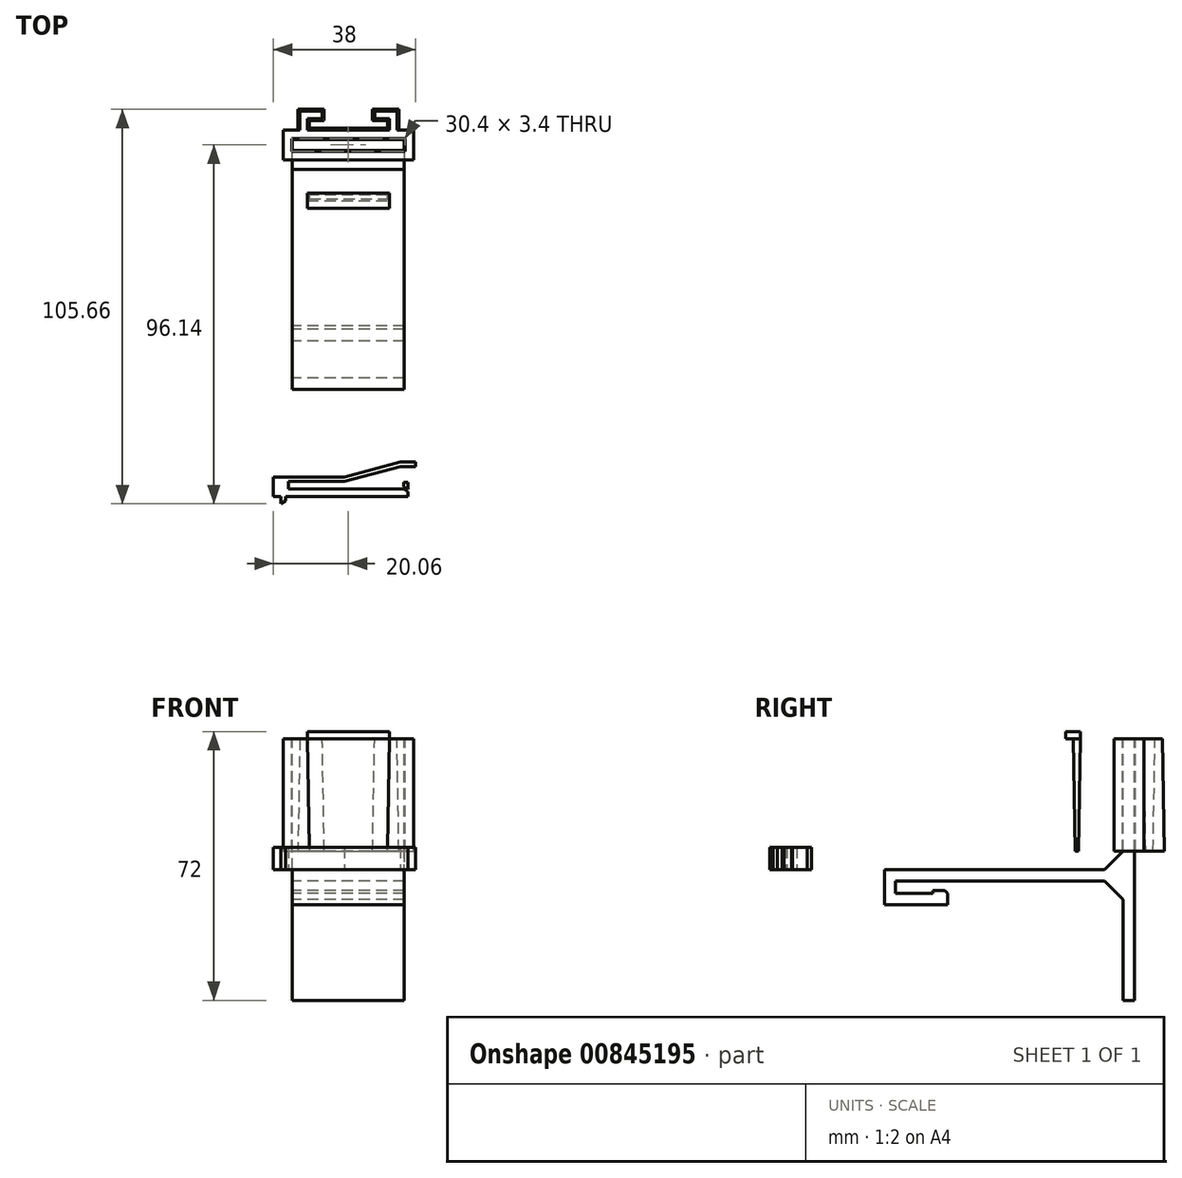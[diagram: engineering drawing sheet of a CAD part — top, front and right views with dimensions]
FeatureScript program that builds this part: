
annotation { "Feature Type Name" : "Feature", "Feature Type Description" : "" }
export const myFeature = defineFeature(function(context is Context, id is Id, definition is map)
    precondition{}
    {
        {
            var Q0;
            Q0=qCreatedBy(makeId("Right.planeOp"),FACE);
            var sketch = newSketch(context, id + "F0", { "sketchPlane" : qUnion([Q0])});
            skLineSegment(sketch, "E0.bottom", {"start": v(0, 0) * mm, "end": v(64, 0) * mm});
            skLineSegment(sketch, "E0.top", {"start": v(0, -3) * mm, "end": v(64, -3) * mm});
            skLineSegment(sketch, "E0.left", {"start": v(0, 0) * mm, "end": v(0, -3) * mm});
            skLineSegment(sketch, "E0.right", {"start": v(64, 0) * mm, "end": v(64, -3) * mm});
            skLineSegment(sketch, "E1.bottom", {"start": v(64, 0) * mm, "end": v(67, 0) * mm});
            skLineSegment(sketch, "E1.top", {"start": v(64, -35) * mm, "end": v(67, -35) * mm});
            skLineSegment(sketch, "E1.left", {"start": v(64, 0) * mm, "end": v(64, -35) * mm});
            skLineSegment(sketch, "E1.right", {"start": v(67, 0) * mm, "end": v(67, -35) * mm});
            skLineSegment(sketch, "E2.bottom", {"start": v(0, -3) * mm, "end": v(3, -3) * mm});
            skLineSegment(sketch, "E2.top", {"start": v(0, -9.4) * mm, "end": v(3, -9.4) * mm});
            skLineSegment(sketch, "E2.left", {"start": v(0, -3) * mm, "end": v(0, -9.4) * mm});
            skLineSegment(sketch, "E2.right", {"start": v(3, -3) * mm, "end": v(3, -9.4) * mm});
            skLineSegment(sketch, "E3.bottom", {"start": v(3, -9.4) * mm, "end": v(17, -9.4) * mm});
            skLineSegment(sketch, "E3.top", {"start": v(3, -6.4) * mm, "end": v(17, -6.4) * mm});
            skLineSegment(sketch, "E3.left", {"start": v(3, -9.4) * mm, "end": v(3, -6.4) * mm});
            skLineSegment(sketch, "E3.right", {"start": v(17, -9.4) * mm, "end": v(17, -6.4) * mm});
            skLineSegment(sketch, "E4.top", {"start": v(64, 35) * mm, "end": v(67, 35) * mm});
            skLineSegment(sketch, "E4.left", {"start": v(64, 0) * mm, "end": v(64, 35) * mm});
            skLineSegment(sketch, "E4.right", {"start": v(67, 0) * mm, "end": v(67, 35) * mm});
            skLineSegment(sketch, "E5.bottom", {"start": v(64, 0) * mm, "end": v(59, 0) * mm});
            skLineSegment(sketch, "E5.top", {"start": v(64, 5) * mm, "end": v(59, 5) * mm});
            skLineSegment(sketch, "E5.left", {"start": v(64, 0) * mm, "end": v(64, 5) * mm});
            skLineSegment(sketch, "E5.right", {"start": v(59, 0) * mm, "end": v(59, 5) * mm});
            skLineSegment(sketch, "E6.bottom", {"start": v(17, -6.4) * mm, "end": v(13, -6.4) * mm});
            skLineSegment(sketch, "E6.top", {"start": v(17, -5.6) * mm, "end": v(13, -5.6) * mm});
            skLineSegment(sketch, "E6.left", {"start": v(17, -6.4) * mm, "end": v(17, -5.6) * mm});
            skLineSegment(sketch, "E6.right", {"start": v(13, -6.4) * mm, "end": v(13, -5.6) * mm});
            skLineSegment(sketch, "E7.bottom", {"start": v(64, -3) * mm, "end": v(59, -3) * mm});
            skLineSegment(sketch, "E7.top", {"start": v(64, -8) * mm, "end": v(59, -8) * mm});
            skLineSegment(sketch, "E7.left", {"start": v(64, -3) * mm, "end": v(64, -8) * mm});
            skLineSegment(sketch, "E7.right", {"start": v(59, -3) * mm, "end": v(59, -8) * mm});
            skSolve(sketch);
        }
        {
            var Q0;
            Q0 = qSketchRegion(id + "F0", true);
            extrude(context, id + "F1", {"entities" : qUnion([Q0]), "depth" : 30 * mm, "offsetDistance" : 25 * mm});
        }
        {
            var Q0;
            Q0=qCreatedBy(makeId("Top.planeOp"),FACE);
            cPlane(context, id + "F2", {"entities" : qUnion([Q0]), "cplaneType" : CPlaneType.OFFSET, "offset" : 35 * mm, "width" : 150 * mm, "height" : 150 * mm});
        }
        {
            var Q0;
            Q0=qCreatedBy(id+"F2.planeOp",FACE);
            var sketch = newSketch(context, id + "F3", { "sketchPlane" : qUnion([Q0])});
            skLineSegment(sketch, "E8.0.0", {"start": v(0, 67) * mm, "end": v(0, 64) * mm, "construction": true});
            skLineSegment(sketch, "E8.0.1", {"start": v(0, 64) * mm, "end": v(30, 64) * mm, "construction": true});
            skLineSegment(sketch, "E8.0.2", {"start": v(30, 64) * mm, "end": v(30, 67) * mm, "construction": true});
            skLineSegment(sketch, "E8.0.3", {"start": v(30, 67) * mm, "end": v(0, 67) * mm, "construction": true});
            skLineSegment(sketch, "E9", {"start": v(15, 67) * mm, "end": v(15, 64) * mm, "construction": true});
            skLineSegment(sketch, "E10", {"start": v(0, 65.5) * mm, "end": v(30, 65.5) * mm, "construction": true});
            skLineSegment(sketch, "E11.bottom", {"start": v(-0.2, 67.2) * mm, "end": v(30.2, 67.2) * mm});
            skLineSegment(sketch, "E11.top", {"start": v(-0.2, 63.8) * mm, "end": v(30.2, 63.8) * mm});
            skLineSegment(sketch, "E11.left", {"start": v(-0.2, 67.2) * mm, "end": v(-0.2, 63.8) * mm});
            skLineSegment(sketch, "E11.right", {"start": v(30.2, 67.2) * mm, "end": v(30.2, 63.8) * mm});
            skPoint(sketch, "E11.middle", {"position": v(15, 65.5) * mm});
            skLineSegment(sketch, "E12.bottom", {"start": v(-2.5, 69.5) * mm, "end": v(32.5, 69.5) * mm});
            skLineSegment(sketch, "E12.top", {"start": v(-2.5, 61.5) * mm, "end": v(32.5, 61.5) * mm});
            skLineSegment(sketch, "E12.left", {"start": v(-2.5, 69.5) * mm, "end": v(-2.5, 61.5) * mm});
            skLineSegment(sketch, "E12.right", {"start": v(32.5, 69.5) * mm, "end": v(32.5, 61.5) * mm});
            skLineSegment(sketch, "E13.bottom", {"start": v(4, 50.55) * mm, "end": v(26, 50.55) * mm});
            skLineSegment(sketch, "E13.top", {"start": v(4, 52.55) * mm, "end": v(26, 52.55) * mm});
            skLineSegment(sketch, "E13.left", {"start": v(4, 50.55) * mm, "end": v(4, 52.55) * mm});
            skLineSegment(sketch, "E13.right", {"start": v(26, 50.55) * mm, "end": v(26, 52.55) * mm});
            skPoint(sketch, "E13.middle", {"position": v(15, 51.55) * mm});
            skPoint(sketch, "E13.middle.positionSnap0", {"position": v(15, 61.5) * mm});
            skPoint(sketch, "E13.centerSnap0", {"position": v(15, 61.5) * mm});
            skLineSegment(sketch, "E14.top", {"start": v(4, 48.55) * mm, "end": v(26, 48.55) * mm});
            skLineSegment(sketch, "E14.left", {"start": v(4, 50.55) * mm, "end": v(4, 48.55) * mm});
            skLineSegment(sketch, "E14.right", {"start": v(26, 50.55) * mm, "end": v(26, 48.55) * mm});
            skLineSegment(sketch, "E15.bottom", {"start": v(2, 69.5) * mm, "end": v(4, 69.5) * mm});
            skLineSegment(sketch, "E15.top", {"start": v(2, 72.5) * mm, "end": v(4, 72.5) * mm});
            skLineSegment(sketch, "E15.left", {"start": v(2, 69.5) * mm, "end": v(2, 72.5) * mm});
            skLineSegment(sketch, "E15.right", {"start": v(4, 69.5) * mm, "end": v(4, 72.5) * mm});
            skLineSegment(sketch, "E16.bottom", {"start": v(26, 69.5) * mm, "end": v(28, 69.5) * mm});
            skLineSegment(sketch, "E16.top", {"start": v(26, 72.5) * mm, "end": v(28, 72.5) * mm});
            skLineSegment(sketch, "E16.left", {"start": v(26, 69.5) * mm, "end": v(26, 72.5) * mm});
            skLineSegment(sketch, "E16.right", {"start": v(28, 69.5) * mm, "end": v(28, 72.5) * mm});
            skLineSegment(sketch, "E17.bottom", {"start": v(2, 72.5) * mm, "end": v(8, 72.5) * mm});
            skLineSegment(sketch, "E17.top", {"start": v(2, 74.5) * mm, "end": v(8, 74.5) * mm});
            skLineSegment(sketch, "E17.left", {"start": v(2, 72.5) * mm, "end": v(2, 74.5) * mm});
            skLineSegment(sketch, "E17.right", {"start": v(8, 72.5) * mm, "end": v(8, 74.5) * mm});
            skLineSegment(sketch, "E18.bottom", {"start": v(28, 72.5) * mm, "end": v(22, 72.5) * mm});
            skLineSegment(sketch, "E18.top", {"start": v(28, 74.5) * mm, "end": v(22, 74.5) * mm});
            skLineSegment(sketch, "E18.left", {"start": v(28, 72.5) * mm, "end": v(28, 74.5) * mm});
            skLineSegment(sketch, "E18.right", {"start": v(22, 72.5) * mm, "end": v(22, 74.5) * mm});
            skLineSegment(sketch, "E19.bottom", {"start": v(2, 69.5) * mm, "end": v(28, 69.5) * mm});
            skLineSegment(sketch, "E19.top", {"start": v(2, 68.5) * mm, "end": v(28, 68.5) * mm});
            skLineSegment(sketch, "E19.left", {"start": v(2, 69.5) * mm, "end": v(2, 68.5) * mm});
            skLineSegment(sketch, "E19.right", {"start": v(28, 69.5) * mm, "end": v(28, 68.5) * mm});
            skSolve(sketch);
        }
        {
            var Q0;
            Q0=makeQuery(id+"F3.imprint","IMPRINT",FACE,{"disambiguationData":[TD([[makeQuery(id+"F3.imprint","IMPRINT",EDGE,{"derivedFrom":sQuery(id+"F3.wireOp",EDGE,"E11.bottom")}),1.0]])]});
            var Q1;
            Q1=makeQuery(id+"F3.imprint","IMPRINT",FACE,{"disambiguationData":[TD([[makeQuery(id+"F3.imprint","IMPRINT",EDGE,{"derivedFrom":sQuery(id+"F3.wireOp",EDGE,"E19.top")}),1.0]])]});
            extrude(context, id + "F4", {"entities" : qUnion([Q0, Q1]), "oppositeDirection" : true, "depth" : 30 * mm, "offsetDistance" : 25 * mm});
        }
        {
            var Q0;
            Q0=makeQuery(id+"F1.opExtrude","SWEPT_EDGE",EDGE,{"disambiguationData":[OSD([sQuery(id+"F0.wireOp",EDGE,"E6.top"),sQuery(id+"F0.wireOp",EDGE,"E6.left")])]});
            chamfer(context, id + "F5", {"entities" : qUnion([Q0]), "width" : 0.8 * mm, "tangentPropagation" : true});
        }
        {
            var Q0;
            Q0=makeQuery(id+"F1.opExtrude","SWEPT_EDGE",EDGE,{"disambiguationData":[OSD([sQuery(id+"F0.wireOp",EDGE,"E5.top"),sQuery(id+"F0.wireOp",EDGE,"E5.right")])]});
            var Q1;
            Q1=makeQuery(id+"F1.opExtrude","SWEPT_EDGE",EDGE,{"disambiguationData":[OSD([sQuery(id+"F0.wireOp",EDGE,"E7.top"),sQuery(id+"F0.wireOp",EDGE,"E7.right")])]});
            chamfer(context, id + "F6", {"entities" : qUnion([Q0, Q1]), "width" : 5 * mm, "tangentPropagation" : true});
        }
        {
            var Q0;
            Q0=makeQuery(id+"F3.imprint","IMPRINT",FACE,{"disambiguationData":[TD([[makeQuery(id+"F3.imprint","IMPRINT",EDGE,{"derivedFrom":sQuery(id+"F3.wireOp",EDGE,"E13.bottom")}),1.0]])]});
            var Q1;
            Q1=makeQuery(id+"F3.imprint","IMPRINT",FACE,{"disambiguationData":[TD([[makeQuery(id+"F3.imprint","IMPRINT",EDGE,{"derivedFrom":sQuery(id+"F3.wireOp",EDGE,"E13.top")}),-1.0]])]});
            extrude(context, id + "F7", {"entities" : qUnion([Q0, Q1]), "oppositeDirection" : true, "depth" : 30 * mm, "offsetDistance" : 25 * mm, "hasDraft" : true, "draftAngle" : 1 * degree, "draftPullDirection" : true});
        }
        {
            var Q0;
            Q0=makeQuery(id+"F3.imprint","IMPRINT",FACE,{"disambiguationData":[TD([[makeQuery(id+"F3.imprint","IMPRINT",EDGE,{"derivedFrom":sQuery(id+"F3.wireOp",EDGE,"E13.bottom")}),-1.0]])]});
            var Q1;
            Q1=makeQuery(id+"F3.imprint","IMPRINT",FACE,{"disambiguationData":[TD([[makeQuery(id+"F3.imprint","IMPRINT",EDGE,{"derivedFrom":sQuery(id+"F3.wireOp",EDGE,"E13.top")}),-1.0]])]});
            extrude(context, id + "F8", {"entities" : qUnion([Q0, Q1]), "operationType" : NewBodyOperationType.ADD, "depth" : 2 * mm, "offsetDistance" : 25 * mm});
        }
        {
            var Q0;
            Q0=qCreatedBy(makeId("Top.planeOp"),FACE);
            var sketch = newSketch(context, id + "F9", { "sketchPlane" : qUnion([Q0])});
            skLineSegment(sketch, "E20.bottom", {"start": v(-1.06, -26.64) * mm, "end": v(28.94, -26.64) * mm});
            skLineSegment(sketch, "E20.top", {"start": v(-1.06, -28.64) * mm, "end": v(28.94, -28.64) * mm});
            skLineSegment(sketch, "E20.left", {"start": v(-1.06, -26.64) * mm, "end": v(-1.06, -28.64) * mm});
            skLineSegment(sketch, "E21.left", {"start": v(28.94, -26.64) * mm, "end": v(28.94, -28.64) * mm});
            skLineSegment(sketch, "E22.bottom", {"start": v(-1.06, -28.64) * mm, "end": v(-5.06, -28.64) * mm});
            skLineSegment(sketch, "E22.top", {"start": v(-1.06, -23.44) * mm, "end": v(-5.06, -23.44) * mm});
            skLineSegment(sketch, "E22.left", {"start": v(-1.06, -28.64) * mm, "end": v(-1.06, -23.44) * mm});
            skLineSegment(sketch, "E22.right", {"start": v(-5.06, -28.64) * mm, "end": v(-5.06, -23.44) * mm});
            skLineSegment(sketch, "E23.bottom", {"start": v(-1.06, -23.44) * mm, "end": v(13.94, -23.44) * mm});
            skLineSegment(sketch, "E23.top", {"start": v(-1.06, -24.64) * mm, "end": v(13.94, -24.64) * mm});
            skLineSegment(sketch, "E23.left", {"start": v(-1.06, -23.44) * mm, "end": v(-1.06, -24.64) * mm});
            skLineSegment(sketch, "E23.right", {"start": v(13.94, -23.44) * mm, "end": v(13.94, -24.64) * mm});
            skLineSegment(sketch, "E24.bottom", {"start": v(28.94, -28.64) * mm, "end": v(30.94, -28.64) * mm});
            skLineSegment(sketch, "E24.top", {"start": v(28.94, -26.64) * mm, "end": v(30.94, -26.64) * mm});
            skLineSegment(sketch, "E24.left", {"start": v(28.94, -28.64) * mm, "end": v(28.94, -26.64) * mm});
            skLineSegment(sketch, "E24.right", {"start": v(30.94, -28.64) * mm, "end": v(30.94, -26.64) * mm});
            skLineSegment(sketch, "E25.bottom", {"start": v(28.94, -20.64) * mm, "end": v(32.94, -20.64) * mm});
            skLineSegment(sketch, "E25.top", {"start": v(28.94, -19.44) * mm, "end": v(32.94, -19.44) * mm});
            skLineSegment(sketch, "E25.left", {"start": v(28.94, -20.64) * mm, "end": v(28.94, -19.44) * mm});
            skLineSegment(sketch, "E25.right", {"start": v(32.94, -20.64) * mm, "end": v(32.94, -19.44) * mm});
            skLineSegment(sketch, "E26", {"start": v(13.94, -23.44) * mm, "end": v(28.94, -19.44) * mm});
            skLineSegment(sketch, "E27", {"start": v(13.94, -24.64) * mm, "end": v(28.94, -20.64) * mm});
            skLineSegment(sketch, "E28.bottom", {"start": v(32.94, -20.64) * mm, "end": v(30.94, -20.64) * mm});
            skLineSegment(sketch, "E28.top", {"start": v(32.94, -26.84) * mm, "end": v(30.94, -26.84) * mm});
            skLineSegment(sketch, "E28.left", {"start": v(32.94, -20.64) * mm, "end": v(32.94, -26.84) * mm});
            skLineSegment(sketch, "E28.right", {"start": v(30.94, -20.64) * mm, "end": v(30.94, -26.84) * mm});
            skLineSegment(sketch, "E29", {"start": v(30.94, -24.84) * mm, "end": v(29.74, -24.84) * mm});
            skLineSegment(sketch, "E30", {"start": v(29.74, -24.84) * mm, "end": v(29.74, -26.04) * mm});
            skLineSegment(sketch, "E31", {"start": v(29.74, -26.04) * mm, "end": v(30.94, -26.84) * mm});
            skLineSegment(sketch, "E32", {"start": v(30.94, -27.38) * mm, "end": v(29.82, -26.64) * mm});
            skLineSegment(sketch, "E33.bottom", {"start": v(-5.06, -28.64) * mm, "end": v(-3.06, -28.64) * mm});
            skLineSegment(sketch, "E33.top", {"start": v(-5.06, -30.64) * mm, "end": v(-3.06, -30.64) * mm});
            skLineSegment(sketch, "E33.left", {"start": v(-5.06, -28.64) * mm, "end": v(-5.06, -30.64) * mm});
            skLineSegment(sketch, "E33.right", {"start": v(-3.06, -28.64) * mm, "end": v(-3.06, -30.64) * mm});
            skLineSegment(sketch, "E34", {"start": v(-3.06, -30.64) * mm, "end": v(-1.86, -29.84) * mm});
            skLineSegment(sketch, "E35", {"start": v(-1.86, -29.84) * mm, "end": v(-1.86, -28.64) * mm});
            skSolve(sketch);
        }
        {
            var Q0;
            {var subQ0=sQuery(id+"F9.wireOp",EDGE,"E20.bottom");Q0=makeQuery(id+"F9.imprint","IMPRINT",FACE,{"disambiguationData":[TD([[makeQuery(id+"F9.imprint","IMPRINT",EDGE,{"derivedFrom":subQ0}),-1.0]])]});}
            var Q1;
            {var subQ3=sQuery(id+"F9.wireOp",EDGE,"E22.bottom");Q1=makeQuery(id+"F9.imprint","IMPRINT",FACE,{"disambiguationData":[TD([[makeQuery(id+"F9.imprint","IMPRINT",EDGE,{"derivedFrom":subQ3}),-1.0]])]});}
            var Q2;
            Q2=makeQuery(id+"F9.imprint","IMPRINT",FACE,{"disambiguationData":[TD([[makeQuery(id+"F9.imprint","IMPRINT",EDGE,{"derivedFrom":sQuery(id+"F9.wireOp",EDGE,"E23.bottom")}),-1.0]])]});
            var Q3;
            Q3=makeQuery(id+"F9.imprint","IMPRINT",FACE,{"disambiguationData":[TD([[makeQuery(id+"F9.imprint","IMPRINT",EDGE,{"derivedFrom":sQuery(id+"F9.wireOp",EDGE,"E23.right")}),1.0]])]});
            var Q4;
            {var subQ1=sQuery(id+"F9.wireOp",EDGE,"DjRPTVJ1-Ztja-NuDC-59Em-ZLGQQdQrhBKL.top");Q4=makeQuery(id+"F9.imprint","IMPRINT",FACE,{"disambiguationData":[TD([[makeQuery(id+"F9.imprint","IMPRINT",EDGE,{"derivedFrom":subQ1}),1.0]])]});}
            var Q5;
            Q5=makeQuery(id+"F9.imprint","IMPRINT",FACE,{"disambiguationData":[TD([[makeQuery(id+"F9.imprint","IMPRINT",EDGE,{"derivedFrom":sQuery(id+"F9.wireOp",EDGE,"E24.bottom")}),1.0]])]});
            var Q6;
            {var subQ6=sQuery(id+"F9.wireOp",EDGE,"xbFztl0G-dcwq-toAX-uXaV-ZmudI0XyXKPU");Q6=makeQuery(id+"F9.imprint","IMPRINT",FACE,{"disambiguationData":[TD([[makeQuery(id+"F9.imprint","IMPRINT",EDGE,{"derivedFrom":subQ6}),-1.0]])]});}
            var Q7;
            Q7=makeQuery(id+"F9.imprint","IMPRINT",FACE,{"disambiguationData":[TD([[makeQuery(id+"F9.imprint","IMPRINT",EDGE,{"derivedFrom":sQuery(id+"F9.wireOp",EDGE,"E25.bottom")}),1.0]])]});
            var Q8;
            {var subQ1=sQuery(id+"F9.wireOp",EDGE,"E28.bottom");Q8=makeQuery(id+"F9.imprint","IMPRINT",FACE,{"disambiguationData":[TD([[makeQuery(id+"F9.imprint","IMPRINT",EDGE,{"derivedFrom":subQ1}),1.0]])]});}
            var Q9;
            {var subQ2=sQuery(id+"F9.wireOp",EDGE,"E29");Q9=makeQuery(id+"F9.imprint","IMPRINT",FACE,{"disambiguationData":[TD([[makeQuery(id+"F9.imprint","IMPRINT",EDGE,{"derivedFrom":subQ2}),1.0]])]});}
            var Q10;
            Q10=makeQuery(id+"F9.imprint","IMPRINT",FACE,{"disambiguationData":[TD([[makeQuery(id+"F9.imprint","IMPRINT",EDGE,{"derivedFrom":sQuery(id+"F9.wireOp",EDGE,"E33.bottom")}),-1.0]])]});
            var Q11;
            {var subQ0=sQuery(id+"F9.wireOp",EDGE,"E33.right");Q11=makeQuery(id+"F9.imprint","IMPRINT",FACE,{"disambiguationData":[TD([[makeQuery(id+"F9.imprint","IMPRINT",EDGE,{"derivedFrom":subQ0}),1.0]])]});}
            var Q12;
            {var subQ0=sQuery(id+"F9.wireOp",EDGE,"E28.right");var subQ1=sQuery(id+"F9.wireOp",EDGE,"E24.top");var subQ2=makeQuery(id+"F9.imprint","INTERSECT",VERTEX,{"derivedFrom":[subQ1,subQ0]});Q12=makeQuery(id+"F9.imprint","IMPRINT",FACE,{"disambiguationData":[TD([[makeQuery(id+"F9.imprint","IMPRINT",EDGE,{"disambiguationData":[TD([[subQ2,1.0]])],"derivedFrom":subQ1}),-1.0]])]});}
            extrude(context, id + "F10", {"entities" : qUnion([Q0, Q1, Q2, Q3, Q4, Q5, Q6, Q7, Q8, Q9, Q10, Q11, Q12]), "depth" : 6 * mm, "offsetDistance" : 25 * mm});
        }
        {
            var Q0;
            Q0=makeQuery(id+"F3.imprint","IMPRINT",FACE,{"disambiguationData":[TD([[makeQuery(id+"F3.imprint","IMPRINT",EDGE,{"derivedFrom":sQuery(id+"F3.wireOp",EDGE,"E18.top")}),1.0]])]});
            var Q1;
            {var subQ0=sQuery(id+"F3.wireOp",EDGE,"E16.left");Q1=makeQuery(id+"F3.imprint","IMPRINT",FACE,{"disambiguationData":[TD([[makeQuery(id+"F3.imprint","IMPRINT",EDGE,{"derivedFrom":subQ0}),-1.0]])]});}
            var Q2;
            Q2=makeQuery(id+"F3.imprint","IMPRINT",FACE,{"disambiguationData":[TD([[makeQuery(id+"F3.imprint","IMPRINT",EDGE,{"derivedFrom":sQuery(id+"F3.wireOp",EDGE,"E19.top")}),1.0]])]});
            var Q3;
            Q3=makeQuery(id+"F3.imprint","IMPRINT",FACE,{"disambiguationData":[TD([[makeQuery(id+"F3.imprint","IMPRINT",EDGE,{"derivedFrom":sQuery(id+"F3.wireOp",EDGE,"E17.top")}),-1.0]])]});
            var Q4;
            {var subQ0=sQuery(id+"F3.wireOp",EDGE,"E15.left");Q4=makeQuery(id+"F3.imprint","IMPRINT",FACE,{"disambiguationData":[TD([[makeQuery(id+"F3.imprint","IMPRINT",EDGE,{"derivedFrom":subQ0}),-1.0]])]});}
            extrude(context, id + "F11", {"entities" : qUnion([Q0, Q1, Q2, Q3, Q4]), "operationType" : NewBodyOperationType.ADD, "oppositeDirection" : true, "depth" : 30 * mm, "offsetDistance" : 25 * mm, "hasDraft" : true, "draftAngle" : 1 * degree});
        }
    });
